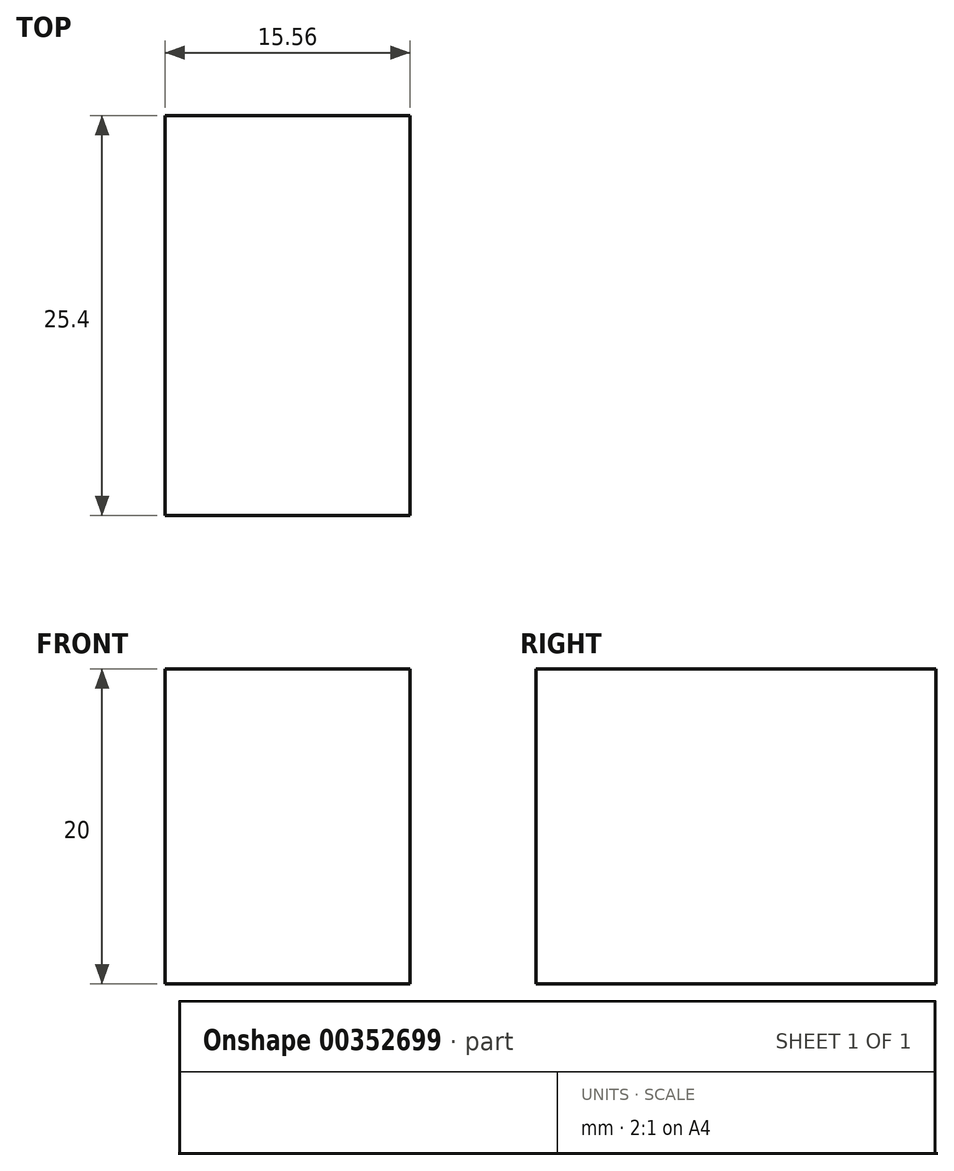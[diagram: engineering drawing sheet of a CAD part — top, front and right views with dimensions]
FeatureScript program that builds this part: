
annotation { "Feature Type Name" : "Feature", "Feature Type Description" : "" }
export const myFeature = defineFeature(function(context is Context, id is Id, definition is map)
    precondition{}
    {
        {
            var Q0;
            Q0=qCreatedBy(makeId("Front.planeOp"),FACE);
            var sketch = newSketch(context, id + "F0", { "sketchPlane" : qUnion([Q0])});
            skLineSegment(sketch, "E0.bottom", {"start": v(57.52, 19.34) * mm, "end": v(41.96, 19.34) * mm});
            skLineSegment(sketch, "E0.top", {"start": v(57.52, -0.66) * mm, "end": v(41.96, -0.66) * mm});
            skLineSegment(sketch, "E0.left", {"start": v(57.52, 19.34) * mm, "end": v(57.52, -0.66) * mm});
            skLineSegment(sketch, "E0.right", {"start": v(41.96, 19.34) * mm, "end": v(41.96, -0.66) * mm});
            skSolve(sketch);
        }
        {
            var Q0;
            Q0=makeQuery(id+"F0.imprint","IMPRINT",FACE,{"disambiguationData":[TD([[makeQuery(id+"F0.imprint","IMPRINT",EDGE,{"derivedFrom":sQuery(id+"F0.wireOp",EDGE,"E0.bottom")}),1.0]])]});
            extrude(context, id + "F1", {"entities" : qUnion([Q0]), "depth" : 25.4 * mm});
        }
    });
